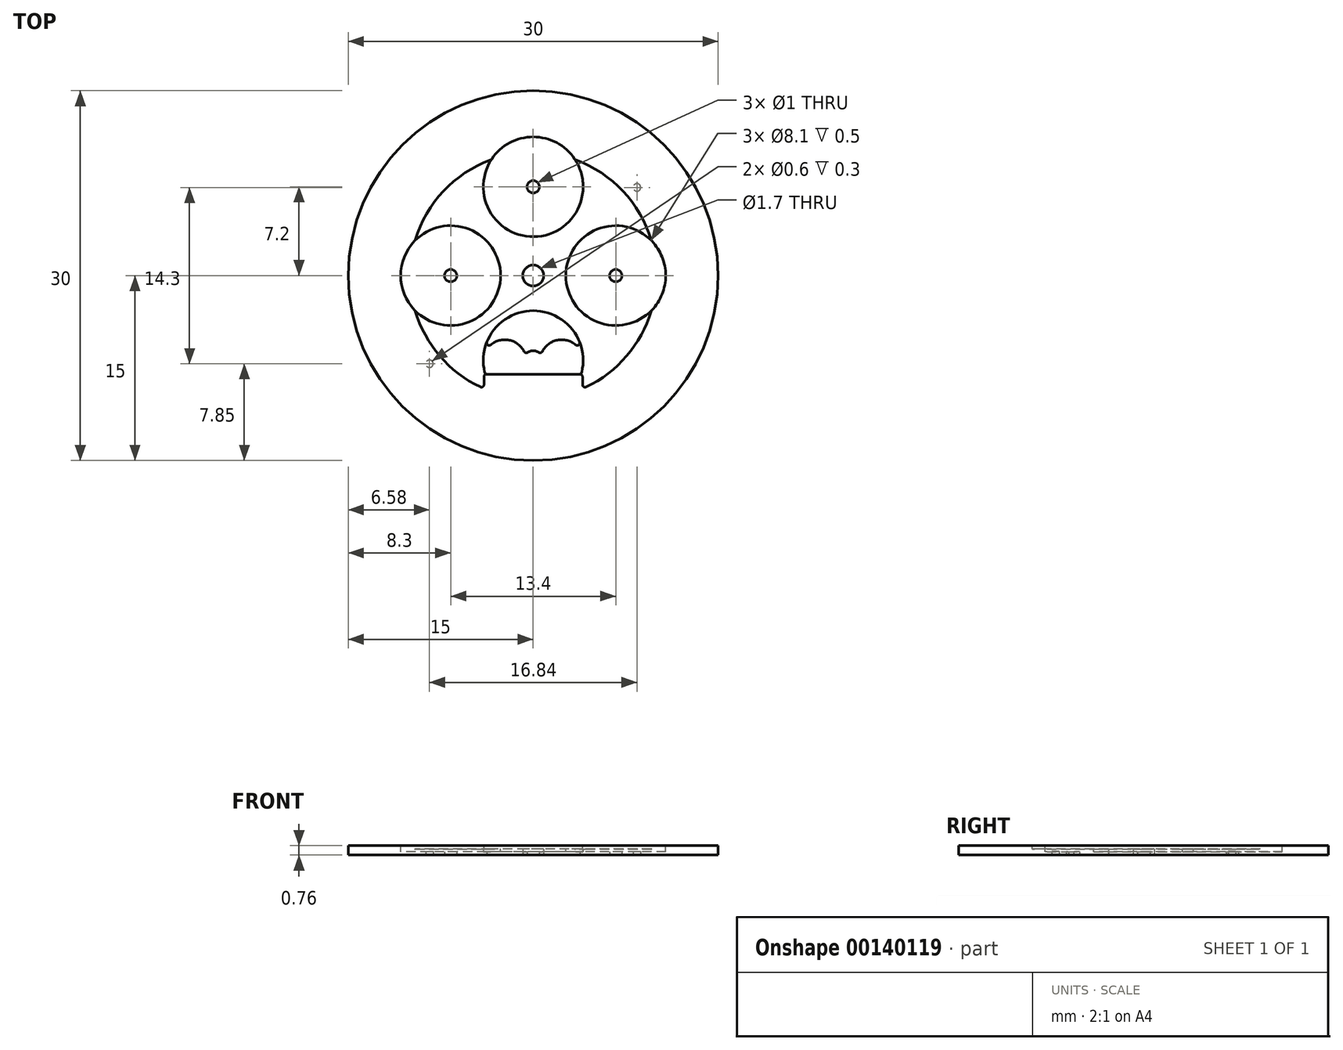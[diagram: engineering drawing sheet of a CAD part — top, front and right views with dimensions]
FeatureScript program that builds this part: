
annotation { "Feature Type Name" : "Feature", "Feature Type Description" : "" }
export const myFeature = defineFeature(function(context is Context, id is Id, definition is map)
    precondition{}
    {
        {
            var Q0;
            Q0=qCreatedBy(makeId("Top.planeOp"),FACE);
            var sketch = newSketch(context, id + "F0", { "sketchPlane" : qUnion([Q0])});
            skCircle(sketch, "E0", {"center": v(0, 0) * mm, "radius": 0.85 * mm});
            skCircle(sketch, "E1", {"center": v(0, 0) * mm, "radius": 15 * mm});
            skCircle(sketch, "E2", {"center": v(0, 7.2) * mm, "radius": 0.5 * mm});
            skCircle(sketch, "E3", {"center": v(6.7, 0) * mm, "radius": 0.5 * mm});
            skCircle(sketch, "E4", {"center": v(-6.7, 0) * mm, "radius": 0.5 * mm});
            skArc(sketch, "E5", {"start": v(0, -2.85) * mm, "mid": v(-2.27, -3.55) * mm, "end": v(-3.76, -5.4) * mm});
            skArc(sketch, "E6", {"start": v(0, -6.1) * mm, "mid": v(-0.23, -6.13) * mm, "end": v(-0.45, -6.24) * mm});
            skArc(sketch, "E7", {"start": v(-0.74, -6.16) * mm, "mid": v(-1.96, -5.23) * mm, "end": v(-3.45, -5.63) * mm});
            skLineSegment(sketch, "E8", {"start": v(0, 0) * mm, "end": v(0, -6.9) * mm, "construction": true});
            skPoint(sketch, "E9.visualSharp", {"position": v(-4.05, -7.05) * mm});
            skArc(sketch, "E9.filletArc", {"start": v(-3.76, -5.4) * mm, "mid": v(-3.7, -5.64) * mm, "end": v(-3.45, -5.63) * mm});
            skPoint(sketch, "E10.visualSharp", {"position": v(-0.63, -6.41) * mm});
            skArc(sketch, "E10.filletArc", {"start": v(-0.74, -6.16) * mm, "mid": v(-0.6, -6.26) * mm, "end": v(-0.45, -6.24) * mm});
            skArc(sketch, "E11.MirrorCS", {"start": v(0.74, -6.16) * mm, "mid": v(0.6, -6.26) * mm, "end": v(0.45, -6.24) * mm});
            skArc(sketch, "E12.MirrorCS", {"start": v(3.76, -5.4) * mm, "mid": v(3.7, -5.64) * mm, "end": v(3.45, -5.63) * mm});
            skArc(sketch, "E13.MirrorCS", {"start": v(0, -6.1) * mm, "mid": v(0.23, -6.13) * mm, "end": v(0.45, -6.24) * mm});
            skPoint(sketch, "E14.MirrorP", {"position": v(0.63, -6.41) * mm});
            skArc(sketch, "E15.MirrorCS", {"start": v(0.74, -6.16) * mm, "mid": v(1.96, -5.23) * mm, "end": v(3.45, -5.63) * mm});
            skArc(sketch, "E16.MirrorCS", {"start": v(0, -2.85) * mm, "mid": v(2.27, -3.55) * mm, "end": v(3.76, -5.4) * mm});
            skSolve(sketch);
        }
        {
            var Q0;
            Q0 = qSketchRegion(id + "F0", true);
            extrude(context, id + "F1", {"entities" : qUnion([Q0]), "depth" : 0.76 * mm});
        }
        {
            var Q0;
            Q0=makeQuery(id+"F1.opExtrude","CAP_FACE",FACE,{"disambiguationData":[OSD([sQuery(id+"F0.wireOp",EDGE,"E0"),sQuery(id+"F0.wireOp",EDGE,"E1"),sQuery(id+"F0.wireOp",EDGE,"E2"),sQuery(id+"F0.wireOp",EDGE,"E3"),sQuery(id+"F0.wireOp",EDGE,"E4"),sQuery(id+"F0.wireOp",EDGE,"E5"),sQuery(id+"F0.wireOp",EDGE,"E6"),sQuery(id+"F0.wireOp",EDGE,"E7"),sQuery(id+"F0.wireOp",EDGE,"E9.filletArc"),sQuery(id+"F0.wireOp",EDGE,"E10.filletArc"),sQuery(id+"F0.wireOp",EDGE,"E11.MirrorCS"),sQuery(id+"F0.wireOp",EDGE,"E12.MirrorCS"),sQuery(id+"F0.wireOp",EDGE,"E13.MirrorCS"),sQuery(id+"F0.wireOp",EDGE,"E15.MirrorCS"),sQuery(id+"F0.wireOp",EDGE,"E16.MirrorCS")])],"isStart":false});
            var sketch = newSketch(context, id + "F2", { "sketchPlane" : qUnion([Q0])});
            skArc(sketch, "E17", {"start": v(4.29, -9.04) * mm, "mid": v(0, 10) * mm, "end": v(-4.29, -9.04) * mm});
            skLineSegment(sketch, "E18", {"start": v(0, -8) * mm, "end": v(-3.8, -8) * mm});
            skPoint(sketch, "E18.startSnap0", {"position": v(0, -6.1) * mm});
            skLineSegment(sketch, "E19", {"start": v(-4, -8.2) * mm, "end": v(-4, -8.85) * mm});
            skLineSegment(sketch, "E20", {"start": v(0, -8) * mm, "end": v(0, -10) * mm, "construction": true});
            skLineSegment(sketch, "E21.MirrorCS", {"start": v(4, -8.2) * mm, "end": v(4, -8.85) * mm});
            skLineSegment(sketch, "E22.MirrorCS", {"start": v(0, -8) * mm, "end": v(3.8, -8) * mm});
            skPoint(sketch, "E23.visualSharp", {"position": v(-4, -8) * mm});
            skArc(sketch, "E23.filletArc", {"start": v(-3.8, -8) * mm, "mid": v(-3.94, -8.06) * mm, "end": v(-4, -8.2) * mm});
            skPoint(sketch, "E24.visualSharp", {"position": v(-4, -9.17) * mm});
            skArc(sketch, "E24.filletArc", {"start": v(-4.29, -9.04) * mm, "mid": v(-4.1, -9.02) * mm, "end": v(-4, -8.85) * mm});
            skPoint(sketch, "E25.visualSharp", {"position": v(4, -8) * mm});
            skArc(sketch, "E25.filletArc", {"start": v(4, -8.2) * mm, "mid": v(3.94, -8.06) * mm, "end": v(3.8, -8) * mm});
            skPoint(sketch, "E26.visualSharp", {"position": v(4, -9.17) * mm});
            skArc(sketch, "E26.filletArc", {"start": v(4, -8.85) * mm, "mid": v(4.1, -9.02) * mm, "end": v(4.29, -9.04) * mm});
            skSolve(sketch);
        }
        {
            var Q0;
            Q0 = qSketchRegion(id + "F2", true);
            extrude(context, id + "F3", {"entities" : qUnion([Q0]), "operationType" : NewBodyOperationType.REMOVE, "oppositeDirection" : true, "depth" : .262 * mm});
        }
        {
            var Q0;
            Q0=makeQuery(id+"F1.opExtrude","CAP_FACE",FACE,{"disambiguationData":[OSD([sQuery(id+"F0.wireOp",EDGE,"E0"),sQuery(id+"F0.wireOp",EDGE,"E1"),sQuery(id+"F0.wireOp",EDGE,"E2"),sQuery(id+"F0.wireOp",EDGE,"E3"),sQuery(id+"F0.wireOp",EDGE,"E4"),sQuery(id+"F0.wireOp",EDGE,"E5"),sQuery(id+"F0.wireOp",EDGE,"E6"),sQuery(id+"F0.wireOp",EDGE,"E7"),sQuery(id+"F0.wireOp",EDGE,"E9.filletArc"),sQuery(id+"F0.wireOp",EDGE,"E10.filletArc"),sQuery(id+"F0.wireOp",EDGE,"E11.MirrorCS"),sQuery(id+"F0.wireOp",EDGE,"E12.MirrorCS"),sQuery(id+"F0.wireOp",EDGE,"E13.MirrorCS"),sQuery(id+"F0.wireOp",EDGE,"E15.MirrorCS"),sQuery(id+"F0.wireOp",EDGE,"E16.MirrorCS")])],"isStart":false});
            var sketch = newSketch(context, id + "F4", { "sketchPlane" : qUnion([Q0])});
            skCircle(sketch, "E27", {"center": v(0, 7.2) * mm, "radius": 4.05 * mm});
            skCircle(sketch, "E28", {"center": v(6.7, 0) * mm, "radius": 4.05 * mm});
            skCircle(sketch, "E29", {"center": v(-6.7, 0) * mm, "radius": 4.05 * mm});
            skArc(sketch, "E30", {"start": v(3.9, -8.02) * mm, "mid": v(0, -2.85) * mm, "end": v(-3.9, -8.02) * mm});
            skLineSegment(sketch, "E31.0", {"start": v(3.8, -8) * mm, "end": v(-3.8, -8) * mm});
            skArc(sketch, "E32.0", {"start": v(-3.8, -8) * mm, "mid": v(-3.85, -8) * mm, "end": v(-3.9, -8.02) * mm});
            skArc(sketch, "E33.0", {"start": v(3.9, -8.02) * mm, "mid": v(3.85, -8) * mm, "end": v(3.8, -8) * mm});
            skPoint(sketch, "E34.orphan", {"position": v(4, -8.2) * mm});
            skPoint(sketch, "E35.orphan", {"position": v(-4, -8.2) * mm});
            skSolve(sketch);
        }
        {
            var Q0;
            Q0 = qSketchRegion(id + "F4", true);
            extrude(context, id + "F5", {"entities" : qUnion([Q0]), "operationType" : NewBodyOperationType.REMOVE, "oppositeDirection" : true, "depth" : .5 * mm});
        }
        {
            var Q0;
            Q0=makeQuery(id+"F5.boolean.opBoolean","INTERSECT",EDGE,{"disambiguationData":[OD(1.0)],"derivedFrom":[makeQuery(id+"F3.boolean.opBoolean","COPY",FACE,{"derivedFrom":makeQuery(id+"F3.opExtrude","SWEPT_FACE",FACE,{"disambiguationData":[OSD([sQuery(id+"F2.wireOp",EDGE,"E17")])]})}),makeQuery(id+"F5.opExtrude","SWEPT_FACE",FACE,{"disambiguationData":[OSD([sQuery(id+"F4.wireOp",EDGE,"E29")])]})]});
            var Q1;
            Q1=makeQuery(id+"F5.boolean.opBoolean","INTERSECT",EDGE,{"disambiguationData":[OD(1.0)],"derivedFrom":[makeQuery(id+"F3.boolean.opBoolean","COPY",FACE,{"derivedFrom":makeQuery(id+"F3.opExtrude","SWEPT_FACE",FACE,{"disambiguationData":[OSD([sQuery(id+"F2.wireOp",EDGE,"E17")])]})}),makeQuery(id+"F5.opExtrude","SWEPT_FACE",FACE,{"disambiguationData":[OSD([sQuery(id+"F4.wireOp",EDGE,"E28")])]})]});
            var Q2;
            Q2=makeQuery(id+"F5.boolean.opBoolean","INTERSECT",EDGE,{"disambiguationData":[OD(0.0)],"derivedFrom":[makeQuery(id+"F3.boolean.opBoolean","COPY",FACE,{"derivedFrom":makeQuery(id+"F3.opExtrude","SWEPT_FACE",FACE,{"disambiguationData":[OSD([sQuery(id+"F2.wireOp",EDGE,"E17")])]})}),makeQuery(id+"F5.opExtrude","SWEPT_FACE",FACE,{"disambiguationData":[OSD([sQuery(id+"F4.wireOp",EDGE,"E28")])]})]});
            var Q3;
            Q3=makeQuery(id+"F5.boolean.opBoolean","COPY",EDGE,{"derivedFrom":makeQuery(id+"F5.opExtrude","SWEPT_EDGE",EDGE,{"disambiguationData":[OSD([sQuery(id+"F2.wireOp",EDGE,"E25.filletArc"),sQuery(id+"F4.wireOp",EDGE,"E30"),sQuery(id+"F4.wireOp",EDGE,"E33.0")])]})});
            var Q4;
            Q4=makeQuery(id+"F5.boolean.opBoolean","COPY",EDGE,{"derivedFrom":makeQuery(id+"F5.opExtrude","SWEPT_EDGE",EDGE,{"disambiguationData":[OSD([sQuery(id+"F2.wireOp",EDGE,"E23.filletArc"),sQuery(id+"F4.wireOp",EDGE,"E30"),sQuery(id+"F4.wireOp",EDGE,"E32.0")])]})});
            var Q5;
            Q5=makeQuery(id+"F5.boolean.opBoolean","INTERSECT",EDGE,{"disambiguationData":[OD(0.0)],"derivedFrom":[makeQuery(id+"F3.boolean.opBoolean","COPY",FACE,{"derivedFrom":makeQuery(id+"F3.opExtrude","SWEPT_FACE",FACE,{"disambiguationData":[OSD([sQuery(id+"F2.wireOp",EDGE,"E17")])]})}),makeQuery(id+"F5.opExtrude","SWEPT_FACE",FACE,{"disambiguationData":[OSD([sQuery(id+"F4.wireOp",EDGE,"E29")])]})]});
            var Q6;
            Q6=makeQuery(id+"F5.boolean.opBoolean","INTERSECT",EDGE,{"disambiguationData":[OD(1.0)],"derivedFrom":[makeQuery(id+"F3.boolean.opBoolean","COPY",FACE,{"derivedFrom":makeQuery(id+"F3.opExtrude","SWEPT_FACE",FACE,{"disambiguationData":[OSD([sQuery(id+"F2.wireOp",EDGE,"E17")])]})}),makeQuery(id+"F5.opExtrude","SWEPT_FACE",FACE,{"disambiguationData":[OSD([sQuery(id+"F4.wireOp",EDGE,"E27")])]})]});
            var Q7;
            Q7=makeQuery(id+"F5.boolean.opBoolean","INTERSECT",EDGE,{"disambiguationData":[OD(0.0)],"derivedFrom":[makeQuery(id+"F3.boolean.opBoolean","COPY",FACE,{"derivedFrom":makeQuery(id+"F3.opExtrude","SWEPT_FACE",FACE,{"disambiguationData":[OSD([sQuery(id+"F2.wireOp",EDGE,"E17")])]})}),makeQuery(id+"F5.opExtrude","SWEPT_FACE",FACE,{"disambiguationData":[OSD([sQuery(id+"F4.wireOp",EDGE,"E27")])]})]});
            fillet(context, id + "F6", {"entities" : qUnion([Q0, Q1, Q2, Q3, Q4, Q5, Q6, Q7]), "radius" : .2 * mm, "tangentPropagation" : true, "allowEdgeOverflow" : false});
        }
        {
            var Q0;
            Q0=makeQuery(id+"F1.opExtrude","CAP_FACE",FACE,{"disambiguationData":[OSD([sQuery(id+"F0.wireOp",EDGE,"E0"),sQuery(id+"F0.wireOp",EDGE,"E1"),sQuery(id+"F0.wireOp",EDGE,"E2"),sQuery(id+"F0.wireOp",EDGE,"E3"),sQuery(id+"F0.wireOp",EDGE,"E4"),sQuery(id+"F0.wireOp",EDGE,"E5"),sQuery(id+"F0.wireOp",EDGE,"E6"),sQuery(id+"F0.wireOp",EDGE,"E7"),sQuery(id+"F0.wireOp",EDGE,"E9.filletArc"),sQuery(id+"F0.wireOp",EDGE,"E10.filletArc"),sQuery(id+"F0.wireOp",EDGE,"E11.MirrorCS"),sQuery(id+"F0.wireOp",EDGE,"E12.MirrorCS"),sQuery(id+"F0.wireOp",EDGE,"E13.MirrorCS"),sQuery(id+"F0.wireOp",EDGE,"E15.MirrorCS"),sQuery(id+"F0.wireOp",EDGE,"E16.MirrorCS")])],"isStart":true});
            var sketch = newSketch(context, id + "F7", { "sketchPlane" : qUnion([Q0])});
            skCircle(sketch, "E36", {"center": v(8.42, -7.15) * mm, "radius": 0.3 * mm});
            skCircle(sketch, "E37", {"center": v(-8.42, 7.15) * mm, "radius": 0.3 * mm});
            skSolve(sketch);
        }
        {
            var Q0;
            Q0 = qSketchRegion(id + "F7", true);
            extrude(context, id + "F8", {"entities" : qUnion([Q0]), "operationType" : NewBodyOperationType.REMOVE, "oppositeDirection" : true, "depth" : .3 * mm});
        }
    });
